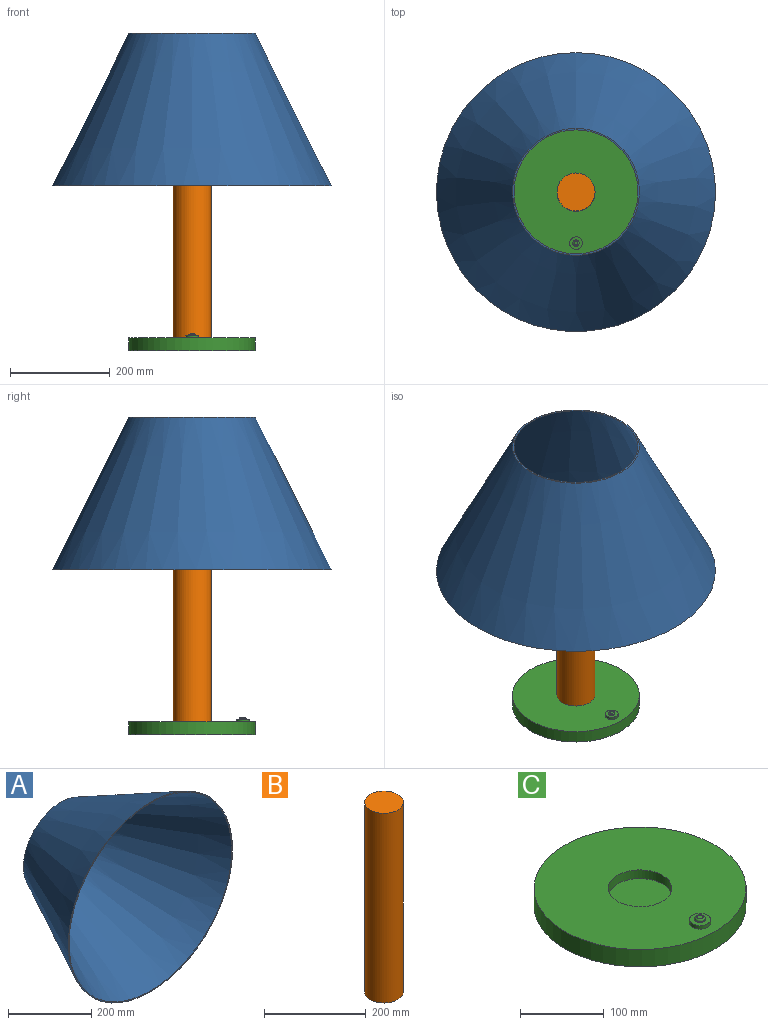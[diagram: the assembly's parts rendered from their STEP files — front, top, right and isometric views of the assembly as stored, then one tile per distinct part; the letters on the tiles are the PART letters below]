
ASSEMBLY  parts=3 mates=3
PART A: 4 faces, bbox 558.8x304.8x558.8 mm
  f0: plane 558.8x558.8mm, normal (0,-1,0), area 4960mm2, adj f1,f3
  f1: cone r=127mm half-angle=26.6deg, axis (0,-1,0), area 435084.4mm2, adj f0,f2
  f2: plane 254x254mm, normal (0,1,0), area 2240.7mm2, adj f1,f3
  f3: cone r=124.73mm half-angle=26.6deg, axis (0,-1,0), area 429003.9mm2, adj f0,f2
PART B: 3 faces, bbox 76.2x76.2x457.2 mm
  f0: cylinder r=38.1mm len=457.2mm, axis (0,0,-1), area 109448.8mm2, adj f1,f2
  f1: plane 76.2x76.2mm, normal (0,0,1), area 4560.4mm2, adj f0
  f2: plane 76.2x76.2mm, normal (0,0,-1), area 4560.4mm2, adj f0
PART C: 10 faces, bbox 254x254x34.3 mm
  f0: cylinder r=127mm len=254mm, axis (0,0,1), area 20268.3mm2, adj f1,f2
  f1: plane 254x254mm, normal (0,0,-1), area 50670.7mm2, adj f0
  f2: plane 254x254mm, normal (0,0,1), area 45603.7mm2, adj f0,f3,f5
  f3: cylinder r=38.1mm len=76.2mm, axis (0,0,1), area 3040.2mm2, adj f2,f4
  f4: plane 76.2x76.2mm, normal (0,0,1), area 4560.4mm2, adj f3
  f5: cylinder r=12.7mm len=25.4mm, axis (0,0,-1), area 405.4mm2, adj f2,f6
  f6: plane 25.4x25.4mm, normal (0,0,1), area 380mm2, adj f5,f7
  f7: cylinder r=6.35mm len=12.7mm, axis (0,0,-1), area 50.7mm2, adj f6,f9
  f8: plane 7.62x7.62mm, normal (0,0,1), area 45.6mm2, adj f9
  f9: torus R=3.81mm, axis (0,0,1), area 136mm2, adj f7,f8
PLACE A rot(axis=(1,0,0),90deg) t=(62.18,7.65,304.8)mm
PLACE B t=(62.18,7.65,0)mm
PLACE C t=(62.18,7.65,0)mm
MATE planar A.f1 <-> B.f0  axis (0,0,-1) through (62.18,7.65,457.2)mm
MATE fastened B.f0 <-> C.f3  axis (0,0,-1) through (62.18,7.65,0)mm
MATE slider A.f1 <-> B.f0  axis (0,0,-1) through (62.18,7.65,609.6)mm
